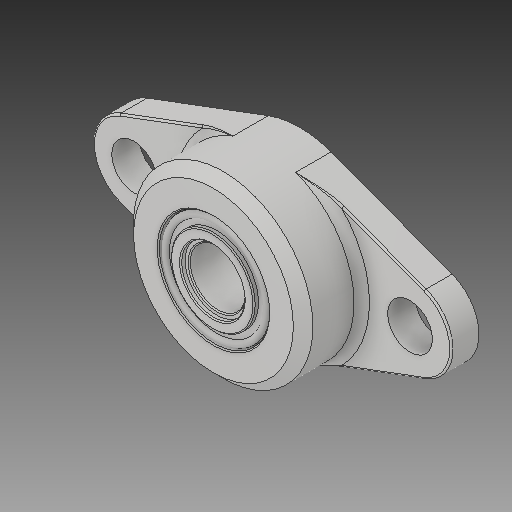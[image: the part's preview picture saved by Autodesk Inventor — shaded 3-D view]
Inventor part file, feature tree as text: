
AUTODESK INVENTOR PART (.ipt)
format: ipt  version: 2019 (Build 230136000, 136)  size: 279,040 bytes
history: mixed  units: in
note: dims shown in document units (in); Inventor stores cm internally (conversion verified against a paired STEP export)
features: chamfer x2, imported_body x1
ambient origin geometry x8: Origin, YZ Plane, XZ Plane, XY Plane, X Axis, Y Axis, Z Axis, Center Point
bodies: Solid1 (imported_parasolid), Solid2 (imported_parasolid)
feature tree (3):
  chamfer  "Chamfer2"  [1 undecoded]
  chamfer  "Chamfer3"  [1 undecoded]
  imported_body  NMx_Import_Brep_tag  [imported B-rep: ~11 faces, bbox_mm=None]
note: 2 required parameter values undecoded (feature->parameter linkage not recoverable at this tier; creation-order binding heuristic only, values carry confidence <= 0.55)
